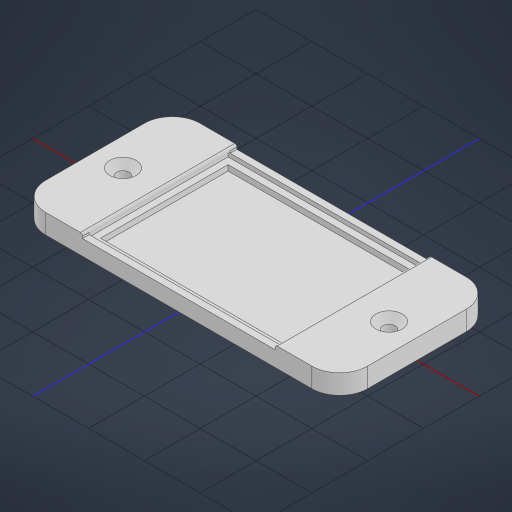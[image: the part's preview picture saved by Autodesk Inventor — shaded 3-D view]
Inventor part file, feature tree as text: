
AUTODESK INVENTOR PART (.ipt)
format: ipt  version: 2023.2 (Build 272271030, 271C)  size: 286,720 bytes
history: native  units: mm
features: extrude x5, sketch x2, hole x1, other x1
ambient origin geometry x8: Origin, YZ Plane, XZ Plane, XY Plane, X Axis, Y Axis, Z Axis, Center Point
bodies: Volumenkörper1 (feature_tree)
feature tree (9):
  extrude  "Extrusion1"  Depth=50.5mm
  extrude  "Extrusion2"  Depth=2.4mm
  extrude  "Extrusion3"  Depth=4.0mm
  sketch  "Skizze2"  dims[d0=70.5mm d1=50.5mm]
  extrude  "Extrusion4"  Depth=4.0mm
  extrude  "Extrusion5"  Depth=2.0mm TaperAngle=0.0deg
  hole  "Bohrung1"  [1 undecoded]
  sketch  "Skizze3"  dims[d2=2.4mm d3=2.4mm d4=4.0mm d7=4.0mm d8=2.0mm d9=0.0mm d10=5.0mm d11=0.0mm d12=2.0mm d13=0.0mm d14=1.5mm d15=1.5mm d16=50.5mm d17=0.0mm d18=4.5mm d19=6.0mm d20=9.4mm d21=2.0mm d22=90.0deg d23=6.0mm d24=0.0mm d25=0.0mm d26=0.0mm d28=20.0mm d29=20.0mm d30=10.0mm d31=10.0mm d32=10.0mm d33=10.0mm]
  other  "Schnittkanten projizieren1"
note: 1 required parameter value undecoded (feature->parameter linkage not recoverable at this tier; creation-order binding heuristic only, values carry confidence <= 0.55)
